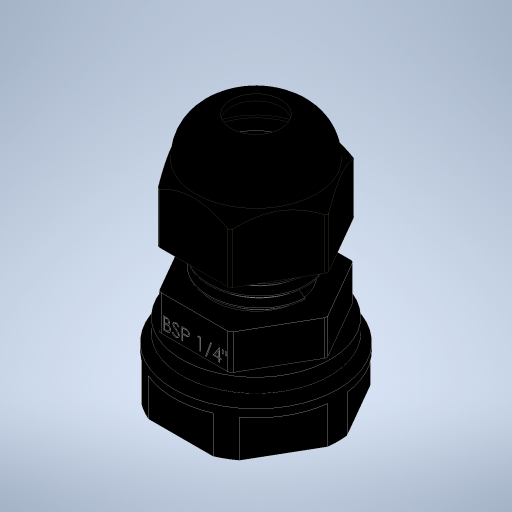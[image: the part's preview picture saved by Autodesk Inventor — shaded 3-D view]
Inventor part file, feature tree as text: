
AUTODESK INVENTOR PART (.ipt)
format: ipt  version: 2024 (Build 280153000, 153)  size: 851,968 bytes
history: native  units: in
note: dims shown in document units (in); Inventor stores cm internally (conversion verified against a paired STEP export)
features: sketch x2, other x2
ambient origin geometry x8: Origin, YZ Plane, XZ Plane, XY Plane, X Axis, Y Axis, Z Axis, Center Point
bodies: Solid1 (feature_tree), Solid2 (feature_tree)
feature tree (4):
  sketch  "Sketch1"
  sketch  "Sketch2"
  other  "Prensa Cabo 1.4 BSP-1-solid1"
  other  "Prensa Cabo 1.4 BSP-1-solid2"
